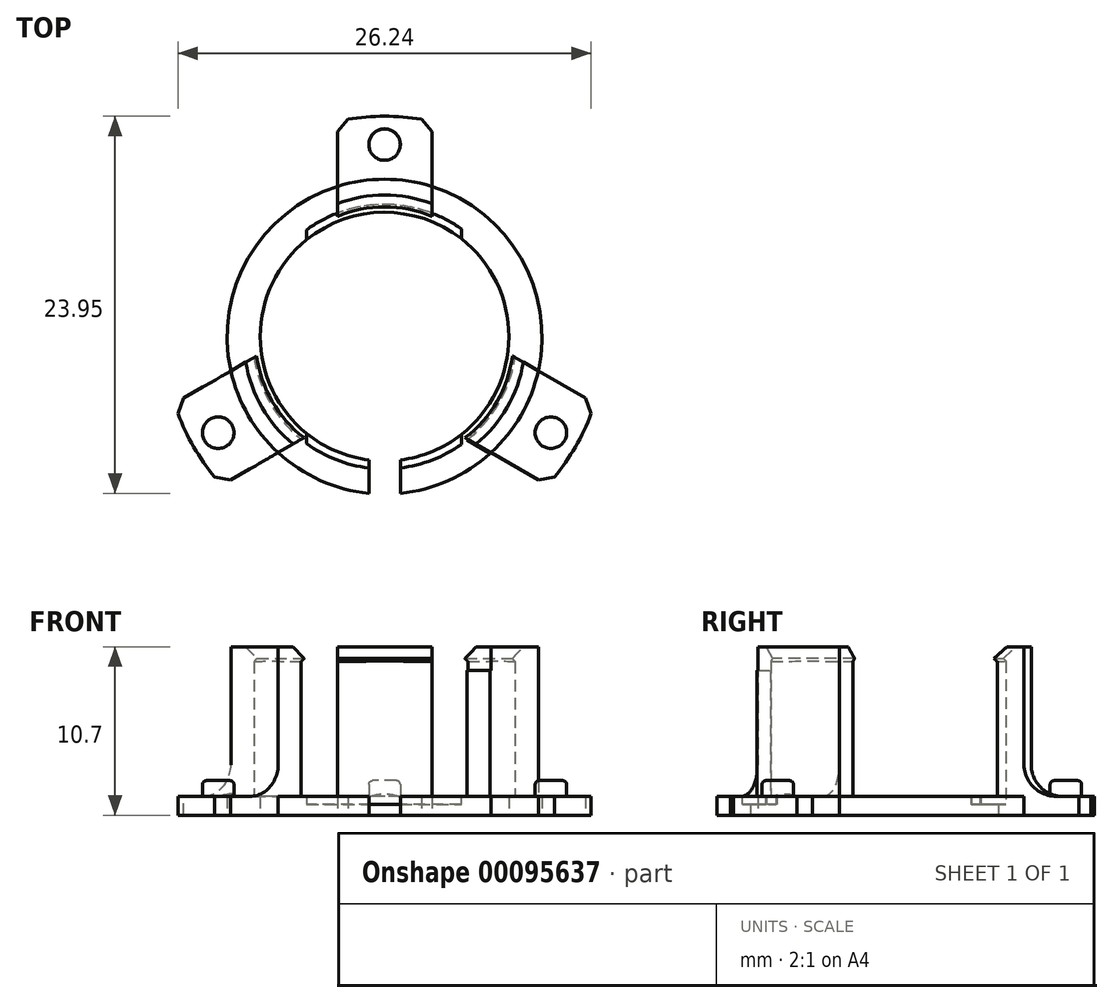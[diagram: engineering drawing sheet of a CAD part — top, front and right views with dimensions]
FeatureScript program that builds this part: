
annotation { "Feature Type Name" : "Feature", "Feature Type Description" : "" }
export const myFeature = defineFeature(function(context is Context, id is Id, definition is map)
    precondition{}
    {
        {
            var Q0;
            Q0=qCreatedBy(makeId("Top.planeOp"),FACE);
            var sketch = newSketch(context, id + "F0", { "sketchPlane" : qUnion([Q0])});
            skArc(sketch, "E0", {"start": v(-3, 9.54) * mm, "mid": v(-8.66, 5) * mm, "end": v(-9.76, -2.17) * mm});
            skCircle(sketch, "E1", {"center": v(0, 0) * mm, "radius": 14 * mm, "construction": true});
            skLineSegment(sketch, "E2", {"start": v(-3, 9.54) * mm, "end": v(-3, 13.67) * mm});
            skLineSegment(sketch, "E3", {"start": v(3, 13.67) * mm, "end": v(3, 9.54) * mm});
            skArc(sketch, "E4", {"start": v(-3, 13.67) * mm, "mid": v(0, 14) * mm, "end": v(3, 13.67) * mm});
            skLineSegment(sketch, "E5.1.0", {"start": v(-6.76, -7.37) * mm, "end": v(-10.34, -9.44) * mm});
            skLineSegment(sketch, "E5.1.1", {"start": v(-13.34, -4.24) * mm, "end": v(-9.76, -2.17) * mm});
            skArc(sketch, "E5.1.2", {"start": v(-10.34, -9.44) * mm, "mid": v(-12.12, -7) * mm, "end": v(-13.34, -4.24) * mm});
            skLineSegment(sketch, "E5.2.0", {"start": v(9.76, -2.17) * mm, "end": v(13.34, -4.24) * mm});
            skLineSegment(sketch, "E5.2.1", {"start": v(10.34, -9.44) * mm, "end": v(6.76, -7.37) * mm});
            skArc(sketch, "E5.2.2", {"start": v(13.34, -4.24) * mm, "mid": v(12.12, -7) * mm, "end": v(10.34, -9.44) * mm});
            skArc(sketch, "E6.trimOffspring", {"start": v(-6.76, -7.37) * mm, "mid": v(0, -10) * mm, "end": v(6.76, -7.37) * mm});
            skArc(sketch, "E7.trimOffspring", {"start": v(9.76, -2.17) * mm, "mid": v(8.66, 5) * mm, "end": v(3, 9.54) * mm});
            skCircle(sketch, "E8", {"center": v(0, 0) * mm, "radius": 7.9 * mm});
            skSolve(sketch);
        }
        {
            var Q0;
            Q0=qSketchRegion(id+"F0",true);
            extrude(context, id + "F1", {"entities" : qUnion([Q0]), "depth" : 1.2 * mm});
        }
        {
            var Q0;
            Q0=makeQuery(id+"F1.opExtrude","CAP_FACE",FACE,{"disambiguationData":[OSD([sQuery(id+"F0.wireOp",EDGE,"E0"),sQuery(id+"F0.wireOp",EDGE,"E2"),sQuery(id+"F0.wireOp",EDGE,"E3"),sQuery(id+"F0.wireOp",EDGE,"E4"),sQuery(id+"F0.wireOp",EDGE,"E5.1.0"),sQuery(id+"F0.wireOp",EDGE,"E5.1.1"),sQuery(id+"F0.wireOp",EDGE,"E5.1.2"),sQuery(id+"F0.wireOp",EDGE,"E5.2.0"),sQuery(id+"F0.wireOp",EDGE,"E5.2.1"),sQuery(id+"F0.wireOp",EDGE,"E5.2.2"),sQuery(id+"F0.wireOp",EDGE,"E6.trimOffspring"),sQuery(id+"F0.wireOp",EDGE,"E7.trimOffspring"),sQuery(id+"F0.wireOp",EDGE,"E8")])],"isStart":false});
            var sketch = newSketch(context, id + "F2", { "sketchPlane" : qUnion([Q0])});
            skCircle(sketch, "E9", {"center": v(0, 0) * mm, "radius": 10 * mm, "construction": true});
            skArc(sketch, "E10", {"start": v(5.23, -6.57) * mm, "mid": v(7.25, -4.23) * mm, "end": v(8.3, -1.32) * mm});
            skArc(sketch, "E11", {"start": v(6.7, -7.42) * mm, "mid": v(8.64, -5.03) * mm, "end": v(9.76, -2.17) * mm});
            skLineSegment(sketch, "E12", {"start": v(-3, 7.85) * mm, "end": v(-3, 9.54) * mm});
            skLineSegment(sketch, "E13", {"start": v(3, 7.85) * mm, "end": v(3, 9.54) * mm});
            skLineSegment(sketch, "E14", {"start": v(-9.76, -2.17) * mm, "end": v(-8.3, -1.32) * mm});
            skLineSegment(sketch, "E15", {"start": v(-6.76, -7.37) * mm, "end": v(-5.3, -6.52) * mm});
            skLineSegment(sketch, "E16", {"start": v(6.7, -7.42) * mm, "end": v(5.23, -6.57) * mm});
            skLineSegment(sketch, "E17", {"start": v(9.76, -2.17) * mm, "end": v(8.3, -1.32) * mm});
            skArc(sketch, "E18.trimOffspring", {"start": v(3, 7.85) * mm, "mid": v(0, 8.4) * mm, "end": v(-3, 7.85) * mm});
            skArc(sketch, "E19.trimOffspring", {"start": v(3, 9.54) * mm, "mid": v(0, 10) * mm, "end": v(-3, 9.54) * mm});
            skPoint(sketch, "E20.start.orphan", {"position": v(-3, 9.54) * mm});
            skPoint(sketch, "E21.start.orphan", {"position": v(3, 9.54) * mm});
            skArc(sketch, "E22.trimOffspring", {"start": v(-9.76, -2.17) * mm, "mid": v(-8.66, -5) * mm, "end": v(-6.76, -7.37) * mm});
            skArc(sketch, "E23.trimOffspring", {"start": v(-8.3, -1.32) * mm, "mid": v(-7.27, -4.2) * mm, "end": v(-5.3, -6.52) * mm});
            skSolve(sketch);
        }
        {
            var Q0;
            Q0=qSketchRegion(id+"F2",true);
            extrude(context, id + "F3", {"entities" : qUnion([Q0]), "operationType" : NewBodyOperationType.ADD, "depth" : 8 * mm});
        }
        {
            var Q0;
            Q0=makeQuery(id+"F3.opExtrude","CAP_FACE",FACE,{"disambiguationData":[OSD([sQuery(id+"F2.wireOp",EDGE,"E14"),sQuery(id+"F2.wireOp",EDGE,"E15"),sQuery(id+"F2.wireOp",EDGE,"E22.trimOffspring"),sQuery(id+"F2.wireOp",EDGE,"E23.trimOffspring")])],"isStart":false});
            var sketch = newSketch(context, id + "F4", { "sketchPlane" : qUnion([Q0])});
            skLineSegment(sketch, "E24", {"start": v(-3, 9.54) * mm, "end": v(-3, 7.64) * mm});
            skLineSegment(sketch, "E25", {"start": v(3, 9.54) * mm, "end": v(3, 7.64) * mm});
            skArc(sketch, "E26.trimOffspring", {"start": v(3, 9.54) * mm, "mid": v(0, 10) * mm, "end": v(-3, 9.54) * mm});
            skArc(sketch, "E27.trimOffspring", {"start": v(3, 7.64) * mm, "mid": v(0, 8.24) * mm, "end": v(-3, 7.64) * mm});
            skArc(sketch, "E28.1.0", {"start": v(-9.76, -2.17) * mm, "mid": v(-8.66, -5) * mm, "end": v(-6.76, -7.37) * mm});
            skLineSegment(sketch, "E28.1.1", {"start": v(-9.76, -2.17) * mm, "end": v(-8.12, -1.22) * mm});
            skLineSegment(sketch, "E28.1.2", {"start": v(-6.76, -7.37) * mm, "end": v(-5.12, -6.42) * mm});
            skArc(sketch, "E28.1.3", {"start": v(-8.12, -1.22) * mm, "mid": v(-7.14, -4.12) * mm, "end": v(-5.12, -6.42) * mm});
            skArc(sketch, "E28.2.0", {"start": v(6.76, -7.37) * mm, "mid": v(8.66, -5) * mm, "end": v(9.76, -2.17) * mm});
            skLineSegment(sketch, "E28.2.1", {"start": v(6.76, -7.37) * mm, "end": v(5.12, -6.42) * mm});
            skLineSegment(sketch, "E28.2.2", {"start": v(9.76, -2.17) * mm, "end": v(8.12, -1.22) * mm});
            skArc(sketch, "E28.2.3", {"start": v(5.12, -6.42) * mm, "mid": v(7.14, -4.12) * mm, "end": v(8.12, -1.22) * mm});
            skSolve(sketch);
        }
        {
            var Q0;
            Q0=qSketchRegion(id+"F4",true);
            extrude(context, id + "F5", {"entities" : qUnion([Q0]), "operationType" : NewBodyOperationType.ADD, "depth" : 1.5 * mm});
        }
        {
            var Q0;
            Q0=makeQuery(id+"F5.opExtrude","CAP_EDGE",EDGE,{"disambiguationData":[OSD([sQuery(id+"F4.wireOp",EDGE,"E27.trimOffspring")])],"isStart":false});
            var Q1;
            Q1=makeQuery(id+"F5.opExtrude","CAP_EDGE",EDGE,{"disambiguationData":[OSD([sQuery(id+"F4.wireOp",EDGE,"E27.trimOffspring")])],"isStart":true});
            var Q2;
            Q2=makeQuery(id+"F5.opExtrude","CAP_EDGE",EDGE,{"disambiguationData":[OSD([sQuery(id+"F4.wireOp",EDGE,"E28.2.3")])],"isStart":false});
            var Q3;
            Q3=makeQuery(id+"F5.opExtrude","CAP_EDGE",EDGE,{"disambiguationData":[OSD([sQuery(id+"F4.wireOp",EDGE,"E28.2.3")])],"isStart":true});
            var Q4;
            Q4=makeQuery(id+"F5.opExtrude","CAP_EDGE",EDGE,{"disambiguationData":[OSD([sQuery(id+"F4.wireOp",EDGE,"E28.1.3")])],"isStart":false});
            var Q5;
            Q5=makeQuery(id+"F5.opExtrude","CAP_EDGE",EDGE,{"disambiguationData":[OSD([sQuery(id+"F4.wireOp",EDGE,"E28.1.3")])],"isStart":true});
            chamfer(context, id + "F6", {"entities" : qUnion([Q0, Q1, Q2, Q3, Q4, Q5]), "width" : .75 * mm, "tangentPropagation" : true});
        }
        {
            var Q0;
            {var subQ0=sQuery(id+"F0.wireOp",EDGE,"E5.2.2");var subQ1=sQuery(id+"F0.wireOp",EDGE,"E5.2.1");var subQ2=sQuery(id+"F0.wireOp",EDGE,"E5.2.0");Q0=makeQuery(id+"F3.boolean.opBoolean","SPLIT",FACE,{"disambiguationData":[TD([makeQuery(id+"F1.opExtrude","SWEPT_FACE",FACE,{"disambiguationData":[OSD([subQ0])]})])],"derivedFrom":makeQuery(id+"F1.opExtrude","CAP_FACE",FACE,{"disambiguationData":[OSD([sQuery(id+"F0.wireOp",EDGE,"E0"),sQuery(id+"F0.wireOp",EDGE,"E2"),sQuery(id+"F0.wireOp",EDGE,"E3"),sQuery(id+"F0.wireOp",EDGE,"E4"),sQuery(id+"F0.wireOp",EDGE,"E5.1.0"),sQuery(id+"F0.wireOp",EDGE,"E5.1.1"),sQuery(id+"F0.wireOp",EDGE,"E5.1.2"),subQ2,subQ1,subQ0,sQuery(id+"F0.wireOp",EDGE,"E6.trimOffspring"),sQuery(id+"F0.wireOp",EDGE,"E7.trimOffspring"),sQuery(id+"F0.wireOp",EDGE,"E8")])],"isStart":false})});}
            var sketch = newSketch(context, id + "F7", { "sketchPlane" : qUnion([Q0])});
            skCircle(sketch, "E29", {"center": v(0, 12.2) * mm, "radius": 1 * mm});
            skCircle(sketch, "E30.1.0", {"center": v(-10.57, -6.1) * mm, "radius": 1 * mm});
            skCircle(sketch, "E30.2.0", {"center": v(10.57, -6.1) * mm, "radius": 1 * mm});
            skPoint(sketch, "E30.center", {"position": v(0, 0) * mm});
            skCircle(sketch, "E31", {"center": v(0, 0) * mm, "radius": 13.2 * mm, "construction": true});
            skSolve(sketch);
        }
        {
            var Q0;
            Q0=makeQuery(id+"F7.imprint","IMPRINT",FACE,{"disambiguationData":[TD([[makeQuery(id+"F7.imprint","IMPRINT",EDGE,{"derivedFrom":sQuery(id+"F7.wireOp",EDGE,"E29")}),1.0]])]});
            var Q1;
            Q1=makeQuery(id+"F7.imprint","IMPRINT",FACE,{"disambiguationData":[TD([[makeQuery(id+"F7.imprint","IMPRINT",EDGE,{"derivedFrom":sQuery(id+"F7.wireOp",EDGE,"E30.1.0")}),1.0]])]});
            var Q2;
            Q2=makeQuery(id+"F7.imprint","IMPRINT",FACE,{"disambiguationData":[TD([[makeQuery(id+"F7.imprint","IMPRINT",EDGE,{"derivedFrom":sQuery(id+"F7.wireOp",EDGE,"E30.2.0")}),1.0]])]});
            extrude(context, id + "F8", {"entities" : qUnion([Q0, Q1, Q2]), "operationType" : NewBodyOperationType.ADD, "depth" : 1 * mm});
        }
        {
            var Q0;
            Q0=makeQuery(id+"F8.opExtrude","CAP_EDGE",EDGE,{"disambiguationData":[OSD([sQuery(id+"F7.wireOp",EDGE,"E30.1.0")])],"isStart":false});
            var Q1;
            Q1=makeQuery(id+"F8.opExtrude","CAP_EDGE",EDGE,{"disambiguationData":[OSD([sQuery(id+"F7.wireOp",EDGE,"E30.2.0")])],"isStart":false});
            var Q2;
            Q2=makeQuery(id+"F8.opExtrude","CAP_EDGE",EDGE,{"disambiguationData":[OSD([sQuery(id+"F7.wireOp",EDGE,"E29")])],"isStart":false});
            fillet(context, id + "F9", {"entities" : qUnion([Q0, Q1, Q2]), "radius" : .25 * mm, "tangentPropagation" : true, "allowEdgeOverflow" : false});
        }
        {
            var Q0;
            Q0=makeQuery(id+"F3.opExtrude","CAP_EDGE",EDGE,{"disambiguationData":[OSD([sQuery(id+"F2.wireOp",EDGE,"E11")])],"isStart":true});
            var Q1;
            Q1=makeQuery(id+"F3.opExtrude","CAP_EDGE",EDGE,{"disambiguationData":[OSD([sQuery(id+"F2.wireOp",EDGE,"E19.trimOffspring")])],"isStart":true});
            var Q2;
            Q2=makeQuery(id+"F3.opExtrude","CAP_EDGE",EDGE,{"disambiguationData":[OSD([sQuery(id+"F2.wireOp",EDGE,"E22.trimOffspring")])],"isStart":true});
            fillet(context, id + "F10", {"entities" : qUnion([Q0, Q1, Q2]), "radius" : 2 * mm, "tangentPropagation" : true, "allowEdgeOverflow" : false});
        }
        {
            var Q0;
            Q0=makeQuery(id+"F10.opFillet","SPLIT",FACE,{"disambiguationData":[OD(0.0)],"derivedFrom":makeQuery(id+"F1.opExtrude","CAP_FACE",FACE,{"disambiguationData":[OSD([sQuery(id+"F0.wireOp",EDGE,"E0"),sQuery(id+"F0.wireOp",EDGE,"E2"),sQuery(id+"F0.wireOp",EDGE,"E3"),sQuery(id+"F0.wireOp",EDGE,"E4"),sQuery(id+"F0.wireOp",EDGE,"E5.1.0"),sQuery(id+"F0.wireOp",EDGE,"E5.1.1"),sQuery(id+"F0.wireOp",EDGE,"E5.1.2"),sQuery(id+"F0.wireOp",EDGE,"E5.2.0"),sQuery(id+"F0.wireOp",EDGE,"E5.2.1"),sQuery(id+"F0.wireOp",EDGE,"E5.2.2"),sQuery(id+"F0.wireOp",EDGE,"E6.trimOffspring"),sQuery(id+"F0.wireOp",EDGE,"E7.trimOffspring"),sQuery(id+"F0.wireOp",EDGE,"E8")])],"isStart":false})});
            var sketch = newSketch(context, id + "F11", { "sketchPlane" : qUnion([Q0])});
            skArc(sketch, "E32", {"start": v(4.87, 6.84) * mm, "mid": v(-0.05, 8.4) * mm, "end": v(-4.95, 6.78) * mm});
            skLineSegment(sketch, "E33.left", {"start": v(-4.95, 6.78) * mm, "end": v(-4.95, -6.78) * mm});
            skLineSegment(sketch, "E33.right", {"start": v(4.87, 6.46) * mm, "end": v(4.87, -6.84) * mm});
            skPoint(sketch, "E34.bottom.start.orphan", {"position": v(-0.04, 6.62) * mm});
            skPoint(sketch, "E35.endSnap0", {"position": v(0, 8.4) * mm});
            skLineSegment(sketch, "E36", {"start": v(4.87, 6.84) * mm, "end": v(4.87, 6.46) * mm});
            skPoint(sketch, "E35.end.orphan", {"position": v(-4.95, 8.4) * mm});
            skPoint(sketch, "E35.start.orphan", {"position": v(0, 8.4) * mm});
            skPoint(sketch, "E37.orphan", {"position": v(4.87, 8.04) * mm});
            skArc(sketch, "E38.trimOffspring", {"start": v(-4.95, -6.78) * mm, "mid": v(-0.05, -8.4) * mm, "end": v(4.87, -6.84) * mm});
            skSolve(sketch);
        }
        {
            var Q0;
            {var subQ9=sQuery(id+"F11.wireOp",EDGE,"E36");Q0=makeQuery(id+"F11.imprint","IMPRINT",FACE,{"disambiguationData":[TD([[makeQuery(id+"F11.imprint","IMPRINT",EDGE,{"derivedFrom":subQ9}),-1.0]])]});}
            var Q1;
            {var subQ0=sQuery(id+"F11.wireOp",EDGE,"E38.trimOffspring");var subQ4=sQuery(id+"F11.wireOp",EDGE,"E33.right");var subQ5=makeQuery(id+"F11.imprint","INTERSECT",VERTEX,{"derivedFrom":[subQ4,subQ0]});Q1=makeQuery(id+"F11.imprint","IMPRINT",FACE,{"disambiguationData":[TD([[makeQuery(id+"F11.imprint","IMPRINT",EDGE,{"disambiguationData":[TD([[subQ5,1.0]])],"derivedFrom":subQ4}),-1.0]])]});}
            var Q2;
            {var subQ0=sQuery(id+"F11.wireOp",EDGE,"E33.left");var subQ1=makeQuery(id+"F1.opExtrude","CAP_EDGE",EDGE,{"disambiguationData":[OSD([sQuery(id+"F0.wireOp",EDGE,"E8")])],"isStart":false});var subQ2=makeQuery(id+"F11.imprint","INTERSECT",VERTEX,{"disambiguationData":[OD(0.0)],"derivedFrom":[subQ1,subQ0]});Q2=makeQuery(id+"F11.imprint","IMPRINT",FACE,{"disambiguationData":[TD([[makeQuery(id+"F11.imprint","IMPRINT",EDGE,{"disambiguationData":[TD([[subQ2,-1.0]])],"derivedFrom":subQ0}),1.0]])]});}
            extrude(context, id + "F12", {"entities" : qUnion([Q0, Q1, Q2]), "operationType" : NewBodyOperationType.REMOVE, "oppositeDirection" : true, "depth" : .5 * mm});
        }
        {
            var Q0;
            Q0=makeQuery(id+"F1.opExtrude","SWEPT_EDGE",EDGE,{"disambiguationData":[OSD([sQuery(id+"F0.wireOp",EDGE,"E5.1.0"),sQuery(id+"F0.wireOp",EDGE,"E5.1.2")])]});
            var Q1;
            Q1=makeQuery(id+"F1.opExtrude","SWEPT_EDGE",EDGE,{"disambiguationData":[OSD([sQuery(id+"F0.wireOp",EDGE,"E5.2.1"),sQuery(id+"F0.wireOp",EDGE,"E5.2.2")])]});
            var Q2;
            Q2=makeQuery(id+"F1.opExtrude","SWEPT_EDGE",EDGE,{"disambiguationData":[OSD([sQuery(id+"F0.wireOp",EDGE,"E5.2.0"),sQuery(id+"F0.wireOp",EDGE,"E5.2.2")])]});
            var Q3;
            Q3=makeQuery(id+"F1.opExtrude","SWEPT_EDGE",EDGE,{"disambiguationData":[OSD([sQuery(id+"F0.wireOp",EDGE,"E5.1.1"),sQuery(id+"F0.wireOp",EDGE,"E5.1.2")])]});
            var Q4;
            Q4=makeQuery(id+"F1.opExtrude","SWEPT_EDGE",EDGE,{"disambiguationData":[OSD([sQuery(id+"F0.wireOp",EDGE,"E2"),sQuery(id+"F0.wireOp",EDGE,"E4")])]});
            var Q5;
            Q5=makeQuery(id+"F1.opExtrude","SWEPT_EDGE",EDGE,{"disambiguationData":[OSD([sQuery(id+"F0.wireOp",EDGE,"E3"),sQuery(id+"F0.wireOp",EDGE,"E4")])]});
            chamfer(context, id + "F13", {"entities" : qUnion([Q0, Q1, Q2, Q3, Q4, Q5]), "width" : .8 * mm, "tangentPropagation" : true});
        }
        {
            var Q0;
            {var subQ0=sQuery(id+"F0.wireOp",EDGE,"E3");var subQ1=sQuery(id+"F0.wireOp",EDGE,"E5.1.1");var subQ2=sQuery(id+"F0.wireOp",EDGE,"E0");var subQ3=sQuery(id+"F0.wireOp",EDGE,"E2");var subQ4=sQuery(id+"F0.wireOp",EDGE,"E8");var subQ5=sQuery(id+"F0.wireOp",EDGE,"E7.trimOffspring");var subQ6=sQuery(id+"F0.wireOp",EDGE,"E5.2.1");var subQ7=sQuery(id+"F0.wireOp",EDGE,"E6.trimOffspring");var subQ8=sQuery(id+"F0.wireOp",EDGE,"E5.2.0");var subQ9=sQuery(id+"F0.wireOp",EDGE,"E5.1.0");var subQ10=makeQuery(id+"F1.opExtrude","CAP_FACE",FACE,{"disambiguationData":[OSD([subQ2,subQ3,subQ0,sQuery(id+"F0.wireOp",EDGE,"E4"),subQ9,subQ1,sQuery(id+"F0.wireOp",EDGE,"E5.1.2"),subQ8,subQ6,sQuery(id+"F0.wireOp",EDGE,"E5.2.2"),subQ7,subQ5,subQ4])],"isStart":false});Q0=makeQuery(id+"F3.boolean.opBoolean","SPLIT",FACE,{"disambiguationData":[TD([makeQuery(id+"F1.opExtrude","SWEPT_FACE",FACE,{"disambiguationData":[OSD([subQ4])]})])],"derivedFrom":subQ10});}
            var sketch = newSketch(context, id + "F14", { "sketchPlane" : qUnion([Q0])});
            skLineSegment(sketch, "E39.bottom", {"start": v(-1, -6.83) * mm, "end": v(1, -6.83) * mm});
            skLineSegment(sketch, "E39.top", {"start": v(-1, -10.39) * mm, "end": v(1, -10.39) * mm});
            skLineSegment(sketch, "E39.left", {"start": v(-1, -6.83) * mm, "end": v(-1, -10.39) * mm});
            skLineSegment(sketch, "E39.right", {"start": v(1, -6.83) * mm, "end": v(1, -10.39) * mm});
            skSolve(sketch);
        }
        {
            var Q0;
            Q0=qSketchRegion(id+"F14",true);
            extrude(context, id + "F15", {"entities" : qUnion([Q0]), "operationType" : NewBodyOperationType.REMOVE, "endBound" : BoundingType.THROUGH_ALL, "oppositeDirection" : true, "depth" : 25 * mm});
        }
    });
